# Revit family: KingswayGroup_TltRllHldrs_Anti-LigatureToiletRollHolder
name_source: partatom
category: Specialty Equipment
units: mm (PartAtom-declared; Revit-internal decimal feet)

## family parameters
Always vertical = Yes
Cut with Voids When Loaded = No
Part Type = Normal
Room Calculation Point = No
Round Connector Dimension = Use Diameter
Shared = No
Work Plane-Based = No

## types (1)
- KingswayGroup_TltRllHldrs_Anti-LigatureToiletRollHolder
    AssetType = Fixed
    BIMObjectName = KingswayGroup_ToiletRollHolders_Anti-LigatureToiletRollHolder
    Category = Pr_40_20_76_88:Toilet roll holders
    Color = For full range of available finishes and colours, contact Kingsway Group
    Default Elevation = 0 mm  [stored 0 ft]
    Description = Toilet Roll Holders
    DurationUnit = year
    Features = An Anti-Ligature Toilet Roll Holder manufactured from stainless steel for a safe, effective, and highly durable solution for patient accessible toilets. The surface-mounted unit is provided with anti-tamper screws.
    Finish = For full range of available finishes and colours, contact Kingsway Group
    Grade = 316
    HolderMaterial = NBS_Concept
    IfcExportAs = IfcFurnitureType
    IfcExportType = USERDEFINED
    Manufacturer = Kingsway Group
    ManufacturerName = Kingsway Group
    ManufacturerURL = https://kingswaygroupglobal.com
    Material = Stainless Steel
    Model = KG03
    ModelNumber = KG03
    ModelReference = Anti-Ligature Toilet Roll Holder
    Name = ToiletRollHolders_Anti-LigatureToiletRollHolder_KG03_KingswayGroup
    NominalHeight = 241.3 mm
    NominalLength = 165.1 mm  [stored 0.541667 ft]
    NominalWidth = 120.7 mm  [stored 0.395997 ft]
    ProductInformation = https://kingswaygroupglobal.com
    Size = 165.1 x 241.3 x 120.7 mm
    URL = https://kingswaygroupglobal.com
    Uniclass2015Code = Pr_40_20_76_88
    Uniclass2015Title = Toilet roll holders
    Uniclass2015Version = Products v1.36
    Version = 1
    WarrantyDescription = 5-Year Guarantee *For faulty manufacture and not for damage
    WarrantyDurationParts = 5
    WarrantyDurationUnit = year

note: [stored X ft] marks values corroborated as IEEE doubles in the binary element streams (Revit-internal decimal feet)

## geometry (parser evidence)
native form markers: Sweep x2
no freeform markers — native parametric forms only
